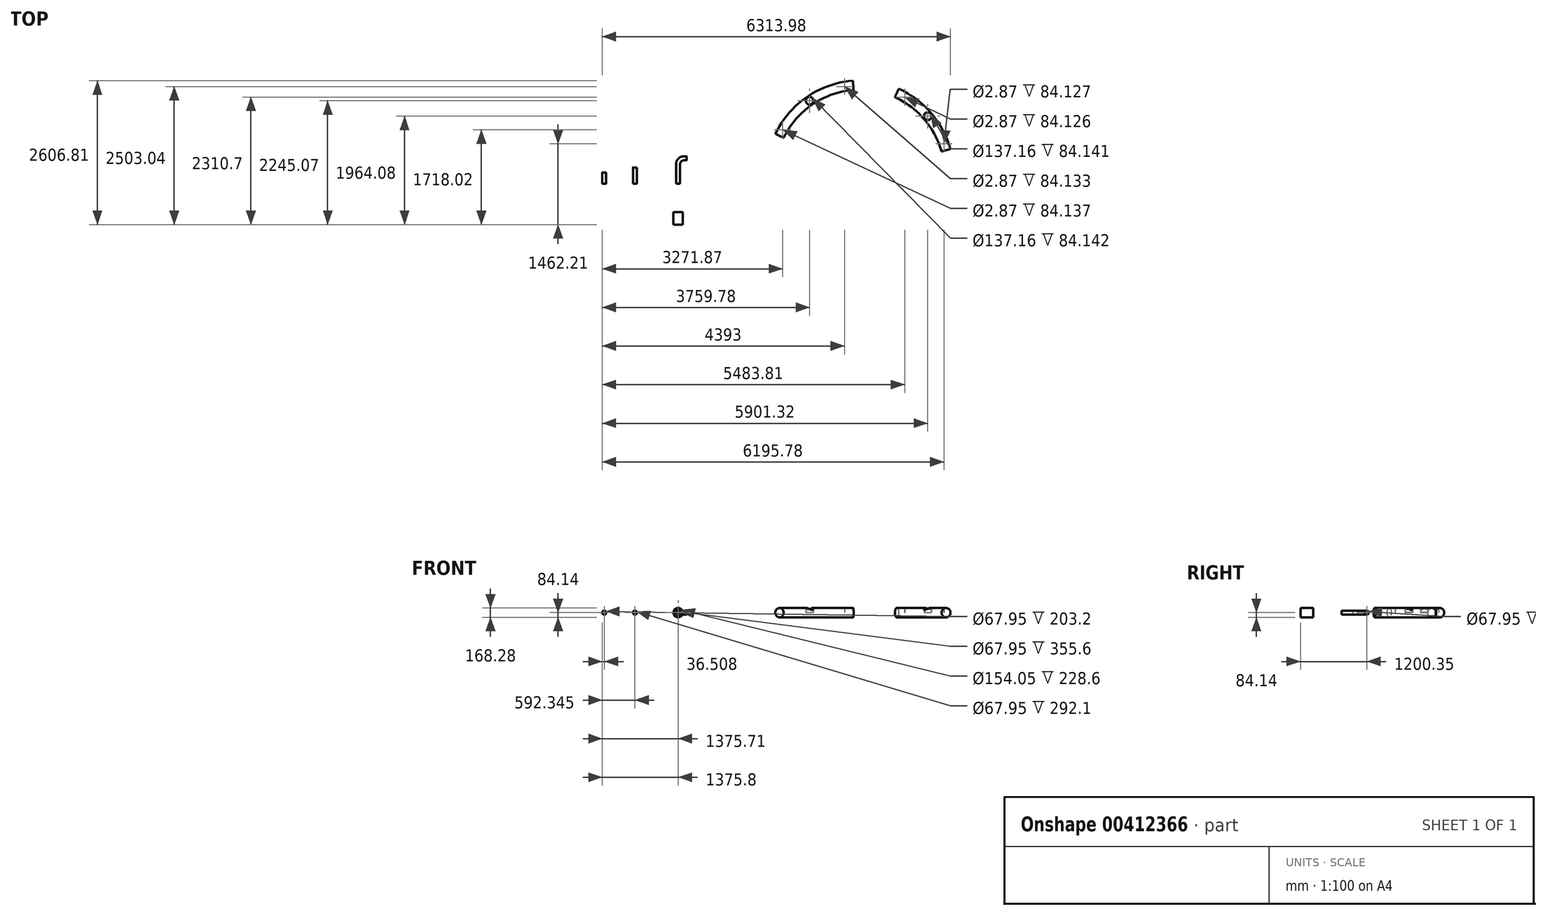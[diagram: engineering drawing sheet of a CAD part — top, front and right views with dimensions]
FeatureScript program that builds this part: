
annotation { "Feature Type Name" : "Feature", "Feature Type Description" : "" }
export const myFeature = defineFeature(function(context is Context, id is Id, definition is map)
    precondition{}
    {
        {
            assignVariable(context, id + "F0", {"name" : "HOLE_DIA", "anyValue" : 2.88});
        }
        {
            var Q0;
            Q0=qCreatedBy(makeId("Top.planeOp"),FACE);
            var sketch = newSketch(context, id + "F1", { "sketchPlane" : qUnion([Q0])});
            skPoint(sketch, "E0", {"position": v(-914.4, 1336.67) * mm});
            skPoint(sketch, "E1", {"position": v(1227.14, 1055.69) * mm});
            skPoint(sketch, "E2.MirrorP", {"position": v(1227.14, -1055.69) * mm});
            skPoint(sketch, "E3.MirrorP", {"position": v(-914.4, -1336.67) * mm});
            skCircle(sketch, "E4", {"center": v(-0.58, 0) * mm, "radius": 1619.19 * mm, "construction": true});
            skSolve(sketch);
        }
        {
            var Q0;
            Q0=qCreatedBy(makeId("Top.planeOp"),FACE);
            var sketch = newSketch(context, id + "F2", { "sketchPlane" : qUnion([Q0])});
            skCircle(sketch, "E5", {"center": v(0, 0) * mm, "radius": 1619.25 * mm, "construction": true});
            skLineSegment(sketch, "E6", {"start": v(2137.22, 0) * mm, "end": v(-2019.73, 0) * mm, "construction": true});
            skLineSegment(sketch, "E7", {"start": v(0, 1894.84) * mm, "end": v(0, -1998.72) * mm, "construction": true});
            skLineSegment(sketch, "E8", {"start": v(0, 0) * mm, "end": v(-1707.7, 985.94) * mm, "construction": true});
            skLineSegment(sketch, "E9", {"start": v(0, 0) * mm, "end": v(1900.22, 691.62) * mm, "construction": true});
            skLineSegment(sketch, "E10", {"start": v(0, 0) * mm, "end": v(966.16, 1673.44) * mm, "construction": true});
            skLineSegment(sketch, "E11", {"start": v(0, 0) * mm, "end": v(-343.97, 1950.77) * mm, "construction": true});
            skLineSegment(sketch, "E12.MirrorCS", {"start": v(0, 0) * mm, "end": v(1900.22, -691.62) * mm, "construction": true});
            skLineSegment(sketch, "E13.MirrorCS", {"start": v(0, 0) * mm, "end": v(966.16, -1673.44) * mm, "construction": true});
            skLineSegment(sketch, "E14.MirrorCS", {"start": v(0, 0) * mm, "end": v(-1707.7, -985.94) * mm, "construction": true});
            skLineSegment(sketch, "E15.MirrorCS", {"start": v(0, 0) * mm, "end": v(-343.97, -1950.77) * mm, "construction": true});
            skPoint(sketch, "E16", {"position": v(-1402.31, 809.62) * mm});
            skPoint(sketch, "E17", {"position": v(-281.18, 1594.65) * mm});
            skPoint(sketch, "E18", {"position": v(809.62, 1402.31) * mm});
            skPoint(sketch, "E19", {"position": v(1521.6, 553.82) * mm});
            skPoint(sketch, "E20.0", {"position": v(-914.4, 1336.67) * mm});
            skLineSegment(sketch, "E21", {"start": v(0, 0) * mm, "end": v(-914.4, 1336.67) * mm, "construction": true});
            skPoint(sketch, "E22.0", {"position": v(1227.14, 1055.69) * mm});
            skLineSegment(sketch, "E23", {"start": v(0, 0) * mm, "end": v(1227.14, 1055.69) * mm, "construction": true});
            skSolve(sketch);
        }
        {
            var Q0;
            Q0=qCreatedBy(makeId("Top.planeOp"),FACE);
            var sketch = newSketch(context, id + "F3", { "sketchPlane" : qUnion([Q0])});
            skCircle(sketch, "E24.0", {"center": v(0, 0) * mm, "radius": 1619.25 * mm});
            skSolve(sketch);
        }
        {
            var Q0;
            Q0=sQuery(id+"F2.wireOp",EDGE,"E5");
            var Q1;
            Q1=sQuery(id+"F1.wireOp",VERTEX,"E0");
            cPlane(context, id + "F4", {"entities" : qUnion([Q0, Q1]), "cplaneType" : CPlaneType.CURVE_POINT, "offset" : 25.4 * mm, "width" : 152.4 * mm, "height" : 152.4 * mm});
        }
        {
            var Q0;
            Q0=sQuery(id+"F2.wireOp",EDGE,"E5");
            var Q1;
            Q1=sQuery(id+"F1.wireOp",VERTEX,"E1");
            cPlane(context, id + "F5", {"entities" : qUnion([Q0, Q1]), "cplaneType" : CPlaneType.CURVE_POINT, "offset" : 25.4 * mm, "width" : 152.4 * mm, "height" : 152.4 * mm});
        }
        {
            var Q0;
            Q0=qCreatedBy(id+"F4.planeOp",FACE);
            var sketch = newSketch(context, id + "F6", { "sketchPlane" : qUnion([Q0])});
            skCircle(sketch, "E25", {"center": v(-1619.25, 0) * mm, "radius": 84.14 * mm});
            skSolve(sketch);
        }
        {
            var Q0;
            Q0=qCreatedBy(id+"F5.planeOp",FACE);
            var sketch = newSketch(context, id + "F7", { "sketchPlane" : qUnion([Q0])});
            skCircle(sketch, "E26", {"center": v(-1619.25, 0) * mm, "radius": 84.14 * mm});
            skSolve(sketch);
        }
        {
            var Q0;
            Q0=makeQuery(id+"F6.imprint","IMPRINT",FACE,{"disambiguationData":[TD([[makeQuery(id+"F6.imprint","IMPRINT",EDGE,{"derivedFrom":sQuery(id+"F6.wireOp",EDGE,"E25")}),1.0]])]});
            var Q1;
            Q1=sQuery(id+"F3.wireOp",EDGE,"E24.0");
            revolve(context, id + "F8", {"entities" : qUnion([Q0]), "axis" : qUnion([Q1]), "revolveType" : RevolveType.SYMMETRIC, "angle" : 60 * degree});
        }
        {
            var Q0;
            Q0=makeQuery(id+"F7.imprint","IMPRINT",FACE,{"disambiguationData":[TD([[makeQuery(id+"F7.imprint","IMPRINT",EDGE,{"derivedFrom":sQuery(id+"F7.wireOp",EDGE,"E26")}),1.0]])]});
            var Q1;
            Q1=sQuery(id+"F2.wireOp",EDGE,"E5");
            revolve(context, id + "F9", {"entities" : qUnion([Q0]), "axis" : qUnion([Q1]), "revolveType" : RevolveType.SYMMETRIC, "angle" : 50 * degree});
        }
        {
            var Q0;
            Q0=sQuery(id+"F2.wireOp",VERTEX,"E16");
            var Q1;
            Q1=sQuery(id+"F2.wireOp",VERTEX,"E17");
            var Q2;
            Q2=makeQuery(id+"F8.opRevolve","SWEPT_BODY",BODY,{"disambiguationData":[OSD([sQuery(id+"F6.wireOp",EDGE,"E25")])]});
            hole(context, id + "F10", {"style" : HoleStyle.SIMPLE, "endStyle" : HoleEndStyle.THROUGH, "oppositeDirection" : true, "holeDiameter" : (getVariable(context, 'HOLE_DIA')) * mm, "isTappedThrough" : true, "tappedDepth" : 12.7 * mm, "tapClearance" : 3, "startFromSketch" : true, "locations" : qUnion([Q0, Q1]), "scope" : qUnion([Q2])});
        }
        {
            var Q0;
            Q0=sQuery(id+"F2.wireOp",VERTEX,"E18");
            var Q1;
            Q1=sQuery(id+"F2.wireOp",VERTEX,"E19");
            var Q2;
            Q2=makeQuery(id+"F9.opRevolve","SWEPT_BODY",BODY,{"disambiguationData":[OSD([sQuery(id+"F7.wireOp",EDGE,"E26")])]});
            hole(context, id + "F11", {"style" : HoleStyle.SIMPLE, "endStyle" : HoleEndStyle.THROUGH, "oppositeDirection" : true, "holeDiameter" : (getVariable(context, 'HOLE_DIA')) * mm, "isTappedThrough" : true, "tappedDepth" : 12.7 * mm, "tapClearance" : 3, "startFromSketch" : true, "locations" : qUnion([Q0, Q1]), "scope" : qUnion([Q2])});
        }
        {
            var Q0;
            Q0=qCreatedBy(makeId("Top.planeOp"),FACE);
            var sketch = newSketch(context, id + "F12", { "sketchPlane" : qUnion([Q0])});
            skLineSegment(sketch, "E27", {"start": v(-3298.38, -165.25) * mm, "end": v(-3298.38, 190.35) * mm});
            skLineSegment(sketch, "E28", {"start": v(-3145.98, 291.95) * mm, "end": v(-3196.78, 291.95) * mm});
            skPoint(sketch, "E29.visualSharp", {"position": v(-3298.38, 291.95) * mm});
            skArc(sketch, "E29.filletArc", {"start": v(-3196.78, 291.95) * mm, "mid": v(-3268.62, 262.2) * mm, "end": v(-3298.38, 190.35) * mm});
            skLineSegment(sketch, "E30", {"start": v(-4081.83, -165.25) * mm, "end": v(-4081.83, 126.85) * mm});
            skLineSegment(sketch, "E31", {"start": v(-4637.67, -165.25) * mm, "end": v(-4637.67, 37.95) * mm});
            skSolve(sketch);
        }
        {
            var Q0;
            Q0=sQuery(id+"F12.wireOp",VERTEX,"E27.start");
            var Q1;
            Q1=sQuery(id+"F12.wireOp",EDGE,"E27");
            cPlane(context, id + "F13", {"entities" : qUnion([Q0, Q1]), "cplaneType" : CPlaneType.LINE_POINT, "offset" : 25.4 * mm, "width" : 152.4 * mm, "height" : 152.4 * mm});
        }
        {
            var Q0;
            Q0=qCreatedBy(id+"F13.planeOp",FACE);
            var sketch = newSketch(context, id + "F14", { "sketchPlane" : qUnion([Q0])});
            skCircle(sketch, "E32", {"center": v(3298.38, 0) * mm, "radius": 36.51 * mm});
            skCircle(sketch, "E33", {"center": v(4081.83, 0) * mm, "radius": 36.51 * mm});
            skCircle(sketch, "E34", {"center": v(4637.67, 0) * mm, "radius": 36.51 * mm});
            skSolve(sketch);
        }
        {
            var Q0;
            Q0=makeQuery(id+"F14.imprint","IMPRINT",FACE,{"disambiguationData":[TD([[makeQuery(id+"F14.imprint","IMPRINT",EDGE,{"derivedFrom":sQuery(id+"F14.wireOp",EDGE,"E32")}),1.0]])]});
            var Q1;
            Q1=sQuery(id+"F12.wireOp",EDGE,"E27");
            var Q2;
            Q2=sQuery(id+"F12.wireOp",EDGE,"E29.filletArc");
            var Q3;
            Q3=sQuery(id+"F12.wireOp",EDGE,"E28");
            sweep(context, id + "F15", {"profiles" : qUnion([Q0]), "path" : qUnion([Q1, Q2, Q3])});
        }
        {
            var Q0;
            Q0=makeQuery(id+"F15.opSweep","CAP_FACE",FACE,{"disambiguationData":[OSD([sQuery(id+"F12.wireOp",VERTEX,"E27.start"),sQuery(id+"F14.wireOp",EDGE,"E32")])],"isStart":true});
            var Q1;
            Q1=makeQuery(id+"F15.opSweep","CAP_FACE",FACE,{"disambiguationData":[OSD([sQuery(id+"F12.wireOp",VERTEX,"E28.start"),sQuery(id+"F14.wireOp",EDGE,"E32")])],"isStart":false});
            shell(context, id + "F16", {"entities" : qUnion([Q0, Q1]), "thickness" : 2.54 * mm});
        }
        {
            var Q0;
            Q0=sQuery(id+"F1.wireOp",VERTEX,"E0");
            var Q1;
            Q1=makeQuery(id+"F8.opRevolve","SWEPT_BODY",BODY,{"disambiguationData":[OSD([sQuery(id+"F6.wireOp",EDGE,"E25")])]});
            hole(context, id + "F17", {"style" : HoleStyle.SIMPLE, "endStyle" : HoleEndStyle.THROUGH, "oppositeDirection" : true, "holeDiameter" : 137.16 * mm, "isTappedThrough" : true, "tappedDepth" : 12.7 * mm, "tapClearance" : 3, "startFromSketch" : true, "locations" : qUnion([Q0]), "scope" : qUnion([Q1]), "majorDiameter" : 6.35 * mm});
        }
        {
            var Q0;
            Q0=sQuery(id+"F1.wireOp",VERTEX,"E1");
            var Q1;
            Q1=makeQuery(id+"F9.opRevolve","SWEPT_BODY",BODY,{"disambiguationData":[OSD([sQuery(id+"F7.wireOp",EDGE,"E26")])]});
            hole(context, id + "F18", {"style" : HoleStyle.SIMPLE, "endStyle" : HoleEndStyle.THROUGH, "oppositeDirection" : true, "holeDiameter" : 137.16 * mm, "isTappedThrough" : true, "tappedDepth" : 12.7 * mm, "tapClearance" : 3, "startFromSketch" : true, "locations" : qUnion([Q0]), "scope" : qUnion([Q1]), "majorDiameter" : 6.35 * mm});
        }
        {
            var Q0;
            Q0=qCreatedBy(makeId("Top.planeOp"),FACE);
            var sketch = newSketch(context, id + "F19", { "sketchPlane" : qUnion([Q0])});
            skLineSegment(sketch, "E35", {"start": v(-3297.95, -679.79) * mm, "end": v(-3297.95, -908.39) * mm});
            skSolve(sketch);
        }
        {
            var Q0;
            Q0=sQuery(id+"F19.wireOp",VERTEX,"E35.end");
            var Q1;
            Q1=sQuery(id+"F19.wireOp",EDGE,"E35");
            cPlane(context, id + "F20", {"entities" : qUnion([Q0, Q1]), "cplaneType" : CPlaneType.LINE_POINT, "offset" : 25.4 * mm, "width" : 152.4 * mm, "height" : 152.4 * mm});
        }
        {
            var Q0;
            Q0=qCreatedBy(id+"F20.planeOp",FACE);
            var sketch = newSketch(context, id + "F21", { "sketchPlane" : qUnion([Q0])});
            skCircle(sketch, "E36", {"center": v(-3298.47, 0) * mm, "radius": 84.14 * mm});
            skSolve(sketch);
        }
        {
            var Q0;
            Q0=makeQuery(id+"F21.imprint","IMPRINT",FACE,{"disambiguationData":[TD([[makeQuery(id+"F21.imprint","IMPRINT",EDGE,{"derivedFrom":sQuery(id+"F21.wireOp",EDGE,"E36")}),1.0]])]});
            var Q1;
            Q1=sQuery(id+"F19.wireOp",EDGE,"E35");
            sweep(context, id + "F22", {"profiles" : qUnion([Q0]), "path" : qUnion([Q1])});
        }
        {
            var Q0;
            Q0=makeQuery(id+"F22.opSweep","CAP_FACE",FACE,{"disambiguationData":[OSD([sQuery(id+"F19.wireOp",VERTEX,"E35.end"),sQuery(id+"F21.wireOp",EDGE,"E36")])],"isStart":true});
            var Q1;
            Q1=makeQuery(id+"F22.opSweep","CAP_FACE",FACE,{"disambiguationData":[OSD([sQuery(id+"F19.wireOp",VERTEX,"E35.start"),sQuery(id+"F21.wireOp",EDGE,"E36")])],"isStart":false});
            shell(context, id + "F23", {"entities" : qUnion([Q0, Q1]), "thickness" : 7.11 * mm});
        }
        {
            var Q0;
            Q0=makeQuery(id+"F14.imprint","IMPRINT",FACE,{"disambiguationData":[TD([[makeQuery(id+"F14.imprint","IMPRINT",EDGE,{"derivedFrom":sQuery(id+"F14.wireOp",EDGE,"E34")}),1.0]])]});
            var Q1;
            Q1=sQuery(id+"F14.wireOp",EDGE,"E34");
            var Q2;
            Q2=sQuery(id+"F12.wireOp",EDGE,"E31");
            sweep(context, id + "F24", {"profiles" : qUnion([Q0]), "surfaceProfiles" : qUnion([Q1]), "path" : qUnion([Q2])});
        }
        {
            var Q0;
            Q0=makeQuery(id+"F24.opSweep","CAP_FACE",FACE,{"disambiguationData":[OSD([sQuery(id+"F12.wireOp",VERTEX,"E31.start"),sQuery(id+"F14.wireOp",EDGE,"E34")])],"isStart":true});
            var Q1;
            Q1=makeQuery(id+"F24.opSweep","CAP_FACE",FACE,{"disambiguationData":[OSD([sQuery(id+"F12.wireOp",VERTEX,"E31.end"),sQuery(id+"F14.wireOp",EDGE,"E34")])],"isStart":false});
            shell(context, id + "F25", {"entities" : qUnion([Q0, Q1]), "thickness" : 2.54 * mm});
        }
        {
            var Q0;
            Q0=makeQuery(id+"F14.imprint","IMPRINT",FACE,{"disambiguationData":[TD([[makeQuery(id+"F14.imprint","IMPRINT",EDGE,{"derivedFrom":sQuery(id+"F14.wireOp",EDGE,"E33")}),1.0]])]});
            var Q1;
            Q1=sQuery(id+"F12.wireOp",EDGE,"E30");
            sweep(context, id + "F26", {"profiles" : qUnion([Q0]), "path" : qUnion([Q1])});
        }
        {
            var Q0;
            Q0=makeQuery(id+"F26.opSweep","CAP_FACE",FACE,{"disambiguationData":[OSD([sQuery(id+"F12.wireOp",VERTEX,"E30.start"),sQuery(id+"F14.wireOp",EDGE,"E33")])],"isStart":true});
            var Q1;
            Q1=makeQuery(id+"F26.opSweep","CAP_FACE",FACE,{"disambiguationData":[OSD([sQuery(id+"F12.wireOp",VERTEX,"E30.end"),sQuery(id+"F14.wireOp",EDGE,"E33")])],"isStart":false});
            shell(context, id + "F27", {"entities" : qUnion([Q0, Q1]), "thickness" : 2.54 * mm});
        }
    });
